# Revit family: P9200
name_source: partatom
category: Generic Models
units: mm (PartAtom-declared; Revit-internal decimal feet)

## family parameters
Can host rebar = No
Cut with Voids When Loaded = No
Part Type = Normal
Room Calculation Point = No
Round Connector Dimension = Use Diameter
Shared = No

## types (3) — shared parameters
Description = P9200 - 1-7/8 x 1-7/8 Telestrut Tubing - GenericModels
H_Half = 0.938 "
Height = 1.875 "
Manufacturer = Atkore Unistrut
Model = P9200
Salsify ID1 = US-P9200
URL = https://www.atkore.com
Unit Weight = 2.245 lb/ft
zero-valued in all types: Default Elevation

## per-type parameters (varying)
| type | Material | UPC-10ft | UPC-20ft |
| P9200 PL | Plain | "786364894058" | "786364894089" |
| P9200 GR | Green | "786364894034" | "786364894065" |
| P9200 PG | Pre-Galvanized | "786364894041" | "786364894072" |

note: column(s) folded — value = type name in every type: Part Number

## geometry (parser evidence)
native form markers: Sweep x16
no freeform markers — native parametric forms only
